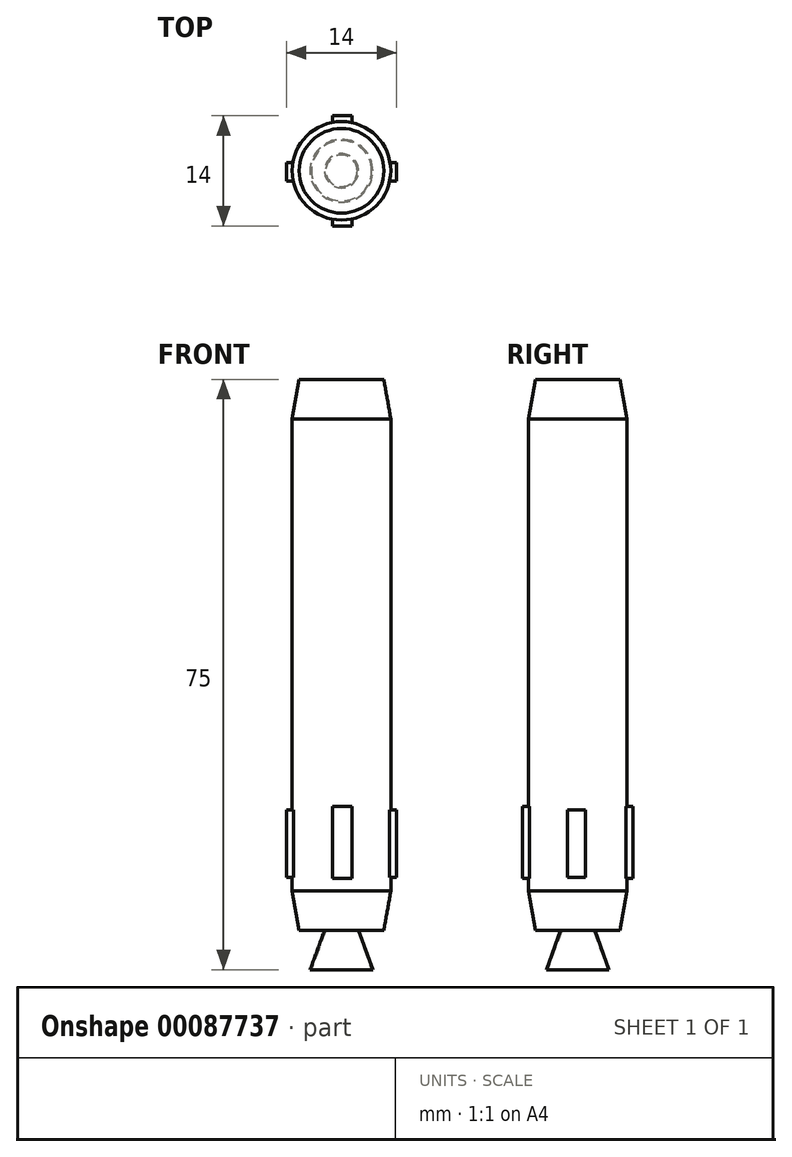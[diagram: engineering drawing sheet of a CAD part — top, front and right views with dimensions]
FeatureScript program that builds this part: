
annotation { "Feature Type Name" : "Feature", "Feature Type Description" : "" }
export const myFeature = defineFeature(function(context is Context, id is Id, definition is map)
    precondition{}
    {
        {
            var Q0;
            Q0=qCreatedBy(makeId("Top.planeOp"),FACE);
            var sketch = newSketch(context, id + "F0", { "sketchPlane" : qUnion([Q0])});
            skCircle(sketch, "E0", {"center": v(0, 0) * mm, "radius": 6.26 * mm});
            skSolve(sketch);
        }
        {
            var Q0;
            Q0 = qSketchRegion(id + "F0", true);
            extrude(context, id + "F1", {"entities" : qUnion([Q0]), "depth" : 10 * mm, "hasSecondDirection" : true, "secondDirectionOppositeDirection" : true, "secondDirectionDepth" : 50 * mm});
        }
        {
            var Q0;
            Q0=makeQuery(id+"F1.opExtrude","CAP_FACE",FACE,{"disambiguationData":[OSD([sQuery(id+"F0.wireOp",EDGE,"E0")])],"isStart":false});
            extrude(context, id + "F2", {"entities" : qUnion([Q0]), "operationType" : NewBodyOperationType.ADD, "depth" : 5 * mm, "hasDraft" : true, "draftAngle" : 10 * degree, "draftPullDirection" : true});
        }
        {
            var Q0;
            Q0=makeQuery(id+"F1.opExtrude","CAP_FACE",FACE,{"disambiguationData":[OSD([sQuery(id+"F0.wireOp",EDGE,"E0")])],"isStart":true});
            extrude(context, id + "F3", {"entities" : qUnion([Q0]), "operationType" : NewBodyOperationType.ADD, "depth" : 5 * mm, "hasDraft" : true, "draftAngle" : 10 * degree, "draftPullDirection" : true});
        }
        {
            var Q0;
            Q0=makeQuery(id+"F3.opExtrude","CAP_FACE",FACE,{"disambiguationData":[OSD([sQuery(id+"F0.wireOp",EDGE,"E0")])],"isStart":false});
            var sketch = newSketch(context, id + "F4", { "sketchPlane" : qUnion([Q0])});
            skCircle(sketch, "E1", {"center": v(0, 0) * mm, "radius": 2.17 * mm});
            skSolve(sketch);
        }
        {
            var Q0;
            Q0 = qSketchRegion(id + "F4", true);
            extrude(context, id + "F5", {"entities" : qUnion([Q0]), "operationType" : NewBodyOperationType.ADD, "depth" : 5 * mm, "hasDraft" : true, "draftAngle" : 20 * degree});
        }
        {
            var Q0;
            Q0=makeQuery(id+"F5.opExtrude","CAP_FACE",FACE,{"disambiguationData":[OSD([sQuery(id+"F4.wireOp",EDGE,"E1")])],"isStart":false});
            var sketch = newSketch(context, id + "F6", { "sketchPlane" : qUnion([Q0])});
            skCircle(sketch, "E2", {"center": v(0, 0) * mm, "radius": 3.83 * mm});
            skSolve(sketch);
        }
        {
            var Q0;
            Q0 = qSketchRegion(id + "F6", true);
            extrude(context, id + "F7", {"entities" : qUnion([Q0]), "operationType" : NewBodyOperationType.REMOVE, "oppositeDirection" : true, "depth" : 5 * mm, "hasDraft" : true, "draftAngle" : 20 * degree, "draftPullDirection" : true});
        }
        {
            var Q0;
            Q0=qCreatedBy(makeId("Front.planeOp"),FACE);
            var sketch = newSketch(context, id + "F8", { "sketchPlane" : qUnion([Q0])});
            skLineSegment(sketch, "E3.bottom", {"start": v(-1.13, -48.36) * mm, "end": v(1.32, -48.36) * mm});
            skLineSegment(sketch, "E3.top", {"start": v(-1.13, -39.25) * mm, "end": v(1.32, -39.25) * mm});
            skLineSegment(sketch, "E3.left", {"start": v(-1.13, -48.36) * mm, "end": v(-1.13, -39.25) * mm});
            skLineSegment(sketch, "E3.right", {"start": v(1.32, -48.36) * mm, "end": v(1.32, -39.25) * mm});
            skSolve(sketch);
        }
        {
            var Q0;
            Q0 = qSketchRegion(id + "F8", true);
            extrude(context, id + "F9", {"entities" : qUnion([Q0]), "operationType" : NewBodyOperationType.ADD, "depth" : 7 * mm, "hasSecondDirection" : true, "secondDirectionOppositeDirection" : true, "secondDirectionDepth" : 7 * mm});
        }
        {
            var Q0;
            Q0=qCreatedBy(makeId("Right.planeOp"),FACE);
            var sketch = newSketch(context, id + "F10", { "sketchPlane" : qUnion([Q0])});
            skLineSegment(sketch, "E4.bottom", {"start": v(1.02, -48.28) * mm, "end": v(-1.3, -48.28) * mm});
            skLineSegment(sketch, "E4.top", {"start": v(1.02, -39.67) * mm, "end": v(-1.3, -39.67) * mm});
            skLineSegment(sketch, "E4.left", {"start": v(1.02, -48.28) * mm, "end": v(1.02, -39.67) * mm});
            skLineSegment(sketch, "E4.right", {"start": v(-1.3, -48.28) * mm, "end": v(-1.3, -39.67) * mm});
            skSolve(sketch);
        }
        {
            var Q0;
            Q0 = qSketchRegion(id + "F10", true);
            extrude(context, id + "F11", {"entities" : qUnion([Q0]), "operationType" : NewBodyOperationType.ADD, "depth" : 7 * mm, "hasSecondDirection" : true, "secondDirectionOppositeDirection" : true, "secondDirectionDepth" : 7 * mm});
        }
    });
